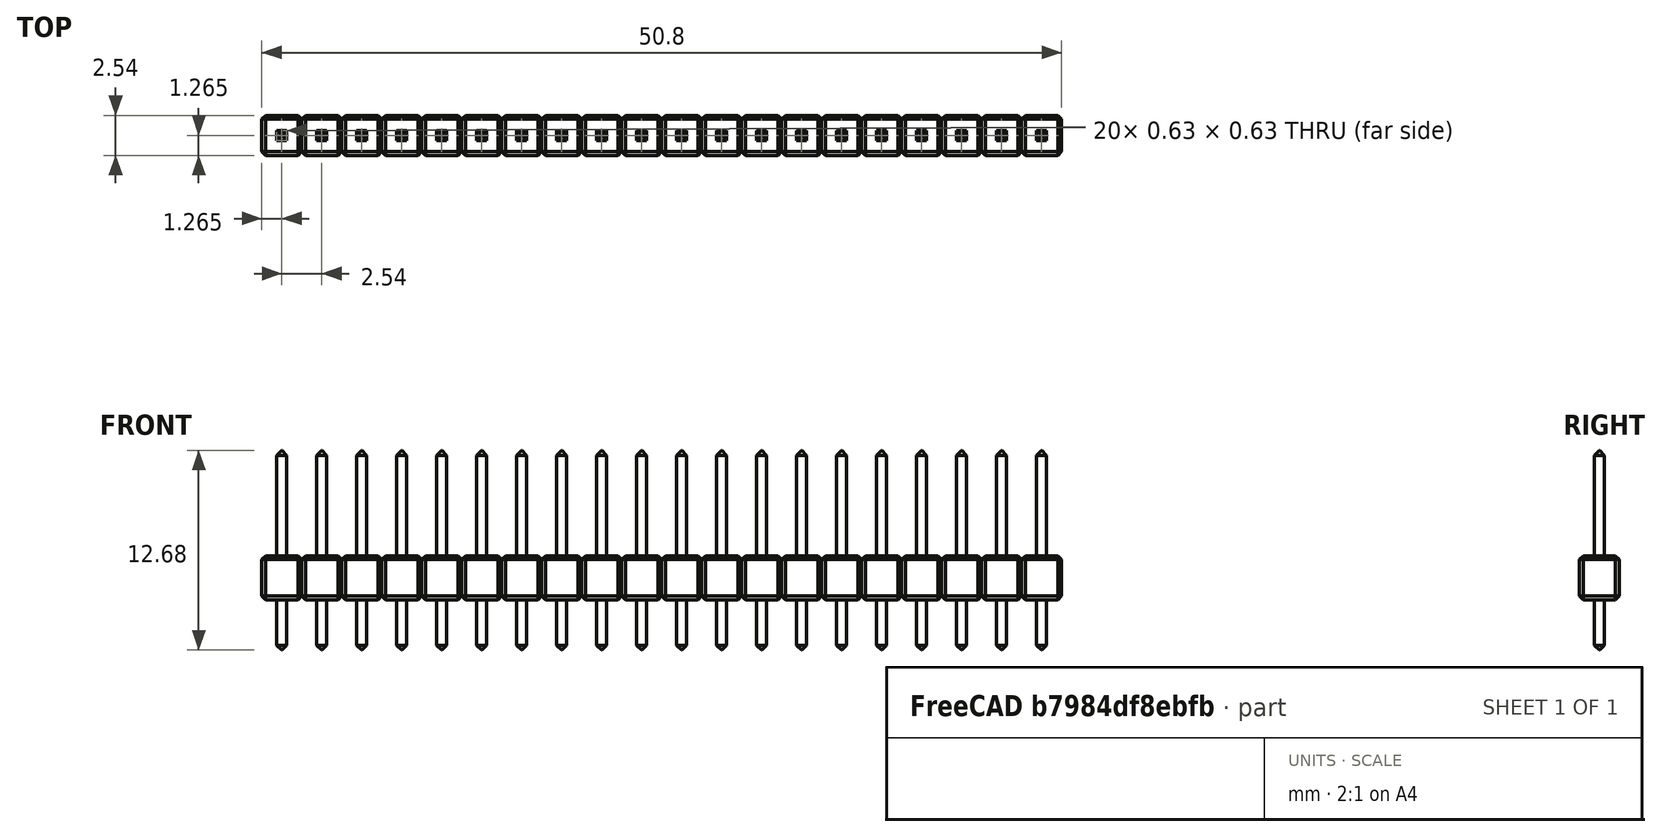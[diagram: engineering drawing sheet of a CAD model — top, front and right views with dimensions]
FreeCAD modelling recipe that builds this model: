
FCSTD DOCUMENT  (FreeCAD 0.18R4 (GitTag))
Label: 20 Pin Header
License: All rights reserved
LicenseURL: http://en.wikipedia.org/wiki/All_rights_reserved
objects: Part::Box×2, Part::Chamfer×2, Part::FeaturePython×2, Part::MultiFuse×1
note: 7 computed .brp shape members not serialized (recipe doc carries the construction recipe); baked Part::Feature solids carry a one-line shape summary decoded from their .brp

FEATURE [Part::Box] Box  label="Cube"
  AttacherType = Attacher::AttachEngine3D
  Height = 2.8
  Length = 2.54
  Width = 2.54
FEATURE [Part::Chamfer] Chamfer  label="Body"
  Base = -> Box
  Edges = 12 edges r=0.25: [Edge1,Edge2,Edge3,Edge4,Edge5,Edge6,Edge7,Edge8,Edge9,Edge10,Edge11,Edge12]
FEATURE [Part::Box] Box001  label="Cube001"
  AttacherType = Attacher::AttachEngine3D
  Height = 12.68
  Length = 0.63
  Placement = pos=(-3,0,0) rot=(0,0,1;0rad)
  Width = 0.63
FEATURE [Part::Chamfer] Chamfer001  label="Pin"
  Base = -> Box001
  Edges = 8 edges r=0.3: [Edge2,Edge4,Edge6,Edge8,Edge9,Edge10,Edge11,Edge12]
  Placement = pos=(3.95,0.95,-3.2) rot=(0,0,1;0rad)
FEATURE [Part::FeaturePython] Array  label="Bodies"  # Draft array (typed FeaturePython)
  Angle = 360
  ArrayType = 0
  Axis = (0,0,1)
  Base = -> Chamfer
  Center = (0,0,0)
  Fuse = false
  IntervalAxis = (0,0,0)
  IntervalX = (2.54,0,0)
  IntervalY = (0,1,0)
  IntervalZ = (0,0,1)
  NumberPolar = 1
  NumberX = 20
  NumberY = 1
  NumberZ = 1
FEATURE [Part::FeaturePython] Array001  label="Pins"  # Draft array (typed FeaturePython)
  Angle = 360
  ArrayType = 0
  Axis = (0,0,1)
  Base = -> Chamfer001
  Center = (0,0,0)
  Fuse = false
  IntervalAxis = (0,0,0)
  IntervalX = (2.54,0,0)
  IntervalY = (0,1,0)
  IntervalZ = (0,0,1)
  NumberPolar = 1
  NumberX = 20
  NumberY = 1
  NumberZ = 1
FEATURE [Part::MultiFuse] Fusion  label="Header"
  Shapes = -> [Array,Array001]
